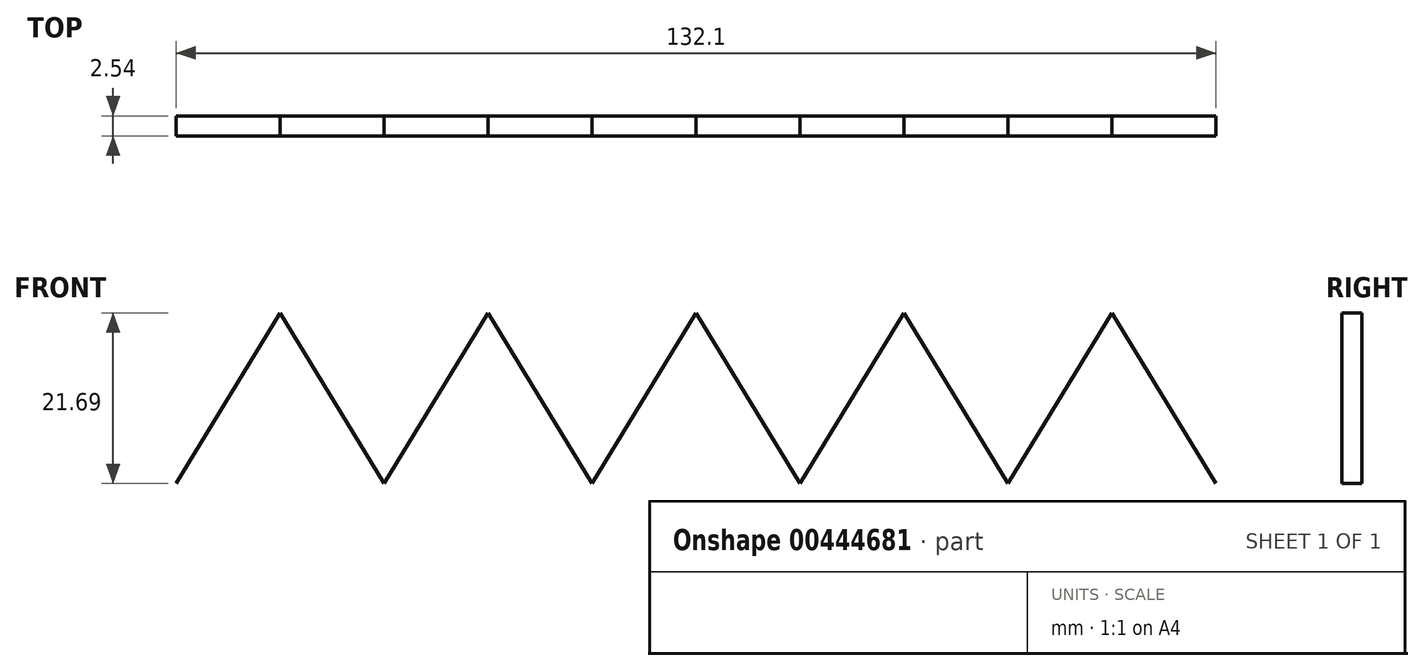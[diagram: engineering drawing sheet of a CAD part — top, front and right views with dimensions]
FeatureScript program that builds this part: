
annotation { "Feature Type Name" : "Feature", "Feature Type Description" : "" }
export const myFeature = defineFeature(function(context is Context, id is Id, definition is map)
    precondition{}
    {
        {
            var Q0;
            Q0=qCreatedBy(makeId("Front.planeOp"),FACE);
            var sketch = newSketch(context, id + "F0", { "sketchPlane" : qUnion([Q0])});
            skLineSegment(sketch, "E0", {"start": v(66.05, 0) * mm, "end": v(52.84, 21.7) * mm});
            skLineSegment(sketch, "E1", {"start": v(52.84, 21.7) * mm, "end": v(39.63, 0) * mm});
            skLineSegment(sketch, "E2", {"start": v(26.42, 21.7) * mm, "end": v(13.21, 0) * mm});
            skLineSegment(sketch, "E3", {"start": v(13.21, 0) * mm, "end": v(0, 21.7) * mm});
            skLineSegment(sketch, "E4", {"start": v(0, 21.7) * mm, "end": v(-13.21, 0) * mm});
            skLineSegment(sketch, "E5", {"start": v(-13.21, 0) * mm, "end": v(-26.42, 21.7) * mm});
            skLineSegment(sketch, "E6", {"start": v(-26.42, 21.7) * mm, "end": v(-39.63, 0) * mm});
            skLineSegment(sketch, "E7", {"start": v(-39.63, 0) * mm, "end": v(-52.84, 21.7) * mm});
            skLineSegment(sketch, "E8", {"start": v(-52.84, 21.7) * mm, "end": v(-66.05, 0) * mm});
            skLineSegment(sketch, "E9", {"start": v(39.63, 0) * mm, "end": v(26.42, 21.7) * mm});
            skSolve(sketch);
        }
        {
            var Q0;
            Q0 = qSketchRegion(id + "F0", true);
            var Q1;
            Q1=sQuery(id+"F0.wireOp",EDGE,"E7");
            var Q2;
            Q2=sQuery(id+"F0.wireOp",EDGE,"E6");
            var Q3;
            Q3=sQuery(id+"F0.wireOp",EDGE,"E5");
            var Q4;
            Q4=sQuery(id+"F0.wireOp",EDGE,"E4");
            var Q5;
            Q5=sQuery(id+"F0.wireOp",EDGE,"E3");
            var Q6;
            Q6=sQuery(id+"F0.wireOp",EDGE,"E9");
            var Q7;
            Q7=sQuery(id+"F0.wireOp",EDGE,"E2");
            var Q8;
            Q8=sQuery(id+"F0.wireOp",EDGE,"E1");
            var Q9;
            Q9=sQuery(id+"F0.wireOp",EDGE,"E0");
            var Q10;
            Q10=sQuery(id+"F0.wireOp",EDGE,"E8");
            extrude(context, id + "F1", {"entities" : qUnion([Q0]), "bodyType" : ToolBodyType.SURFACE, "surfaceEntities" : qUnion([Q1, Q2, Q3, Q4, Q5, Q6, Q7, Q8, Q9, Q10]), "depth" : 2.54 * mm});
        }
    });
